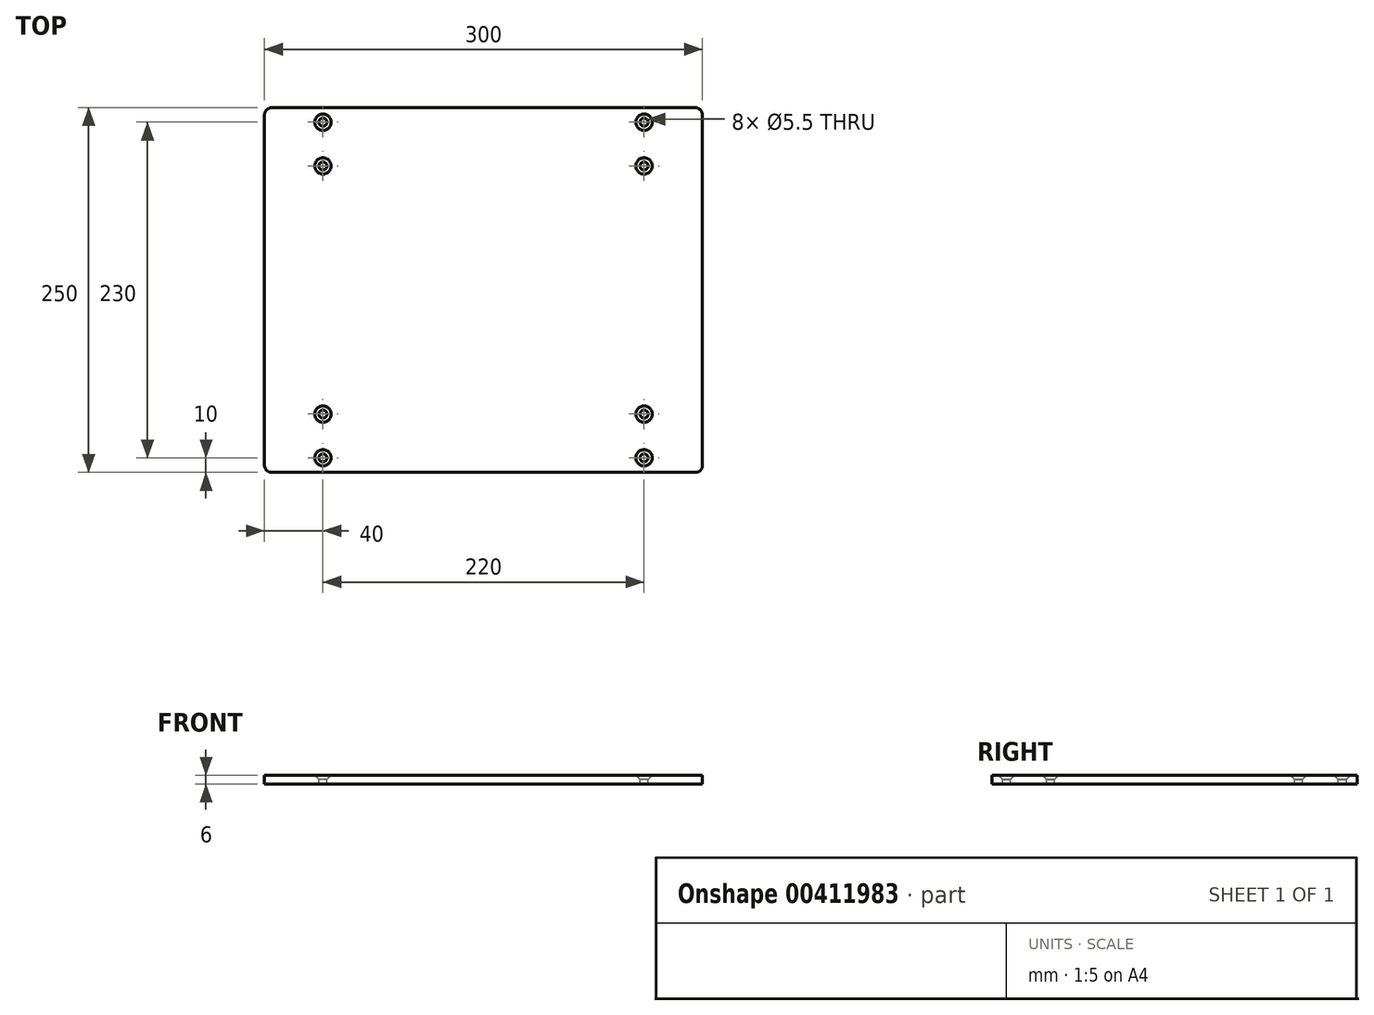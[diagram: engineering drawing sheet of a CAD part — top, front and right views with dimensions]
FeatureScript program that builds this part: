
annotation { "Feature Type Name" : "Feature", "Feature Type Description" : "" }
export const myFeature = defineFeature(function(context is Context, id is Id, definition is map)
    precondition{}
    {
        {
            var Q0;
            Q0=qCreatedBy(makeId("Top.planeOp"),FACE);
            var sketch = newSketch(context, id + "F0", { "sketchPlane" : qUnion([Q0])});
            skLineSegment(sketch, "E0.bottom", {"start": v(150, -125) * mm, "end": v(-150, -125) * mm});
            skLineSegment(sketch, "E0.top", {"start": v(150, 125) * mm, "end": v(-150, 125) * mm});
            skLineSegment(sketch, "E0.left", {"start": v(150, -125) * mm, "end": v(150, 125) * mm});
            skLineSegment(sketch, "E0.right", {"start": v(-150, -125) * mm, "end": v(-150, 125) * mm});
            skPoint(sketch, "E0.middle", {"position": v(0, 0) * mm});
            skLineSegment(sketch, "E1", {"start": v(-110, 125) * mm, "end": v(-110, -125) * mm, "construction": true});
            skLineSegment(sketch, "E2", {"start": v(110, 125) * mm, "end": v(110, -125) * mm, "construction": true});
            skPoint(sketch, "E3", {"position": v(-110, 115) * mm});
            skPoint(sketch, "E4", {"position": v(-110, 85) * mm});
            skPoint(sketch, "E5.MirrorP", {"position": v(110, 115) * mm});
            skPoint(sketch, "E6.MirrorP", {"position": v(110, 85) * mm});
            skPoint(sketch, "E7.MirrorP", {"position": v(-110, -85) * mm});
            skPoint(sketch, "E8.MirrorP", {"position": v(-110, -115) * mm});
            skPoint(sketch, "E9.MirrorP", {"position": v(110, -115) * mm});
            skPoint(sketch, "E10.MirrorP", {"position": v(110, -85) * mm});
            skSolve(sketch);
        }
        {
            var Q0;
            Q0 = qSketchRegion(id + "F0", true);
            extrude(context, id + "F1", {"entities" : qUnion([Q0]), "oppositeDirection" : true, "depth" : 6 * mm, "offsetDistance" : 25 * mm});
        }
        {
            var Q0;
            Q0=sQuery(id+"F0.wireOp",VERTEX,"E3");
            var Q1;
            Q1=sQuery(id+"F0.wireOp",VERTEX,"E4");
            var Q2;
            Q2=sQuery(id+"F0.wireOp",VERTEX,"E5.MirrorP");
            var Q3;
            Q3=sQuery(id+"F0.wireOp",VERTEX,"E6.MirrorP");
            var Q4;
            Q4=sQuery(id+"F0.wireOp",VERTEX,"E10.MirrorP");
            var Q5;
            Q5=sQuery(id+"F0.wireOp",VERTEX,"E9.MirrorP");
            var Q6;
            Q6=sQuery(id+"F0.wireOp",VERTEX,"E8.MirrorP");
            var Q7;
            Q7=sQuery(id+"F0.wireOp",VERTEX,"E7.MirrorP");
            var Q8;
            Q8=makeQuery(id+"F1.opExtrude","SWEPT_BODY",BODY,{"disambiguationData":[OSD([sQuery(id+"F0.wireOp",EDGE,"E0.bottom"),sQuery(id+"F0.wireOp",EDGE,"E0.top"),sQuery(id+"F0.wireOp",EDGE,"E0.left"),sQuery(id+"F0.wireOp",EDGE,"E0.right")])]});
            hole(context, id + "F2", {"style" : HoleStyle.C_SINK, "endStyle" : HoleEndStyle.THROUGH, "standardTappedOrClearance" : lookupTablePath({ "fit" : "Normal", "standard" : "ISO", "size" : "M5", "type" : "Clearance" }), "standardBlindInLast" : lookupTablePath({ "fit" : "Standard", "standard" : "ISO", "size" : "M5", "type" : "Clearance" }), "holeDiameter" : 5.5 * mm, "cSinkDiameter" : 11.2 * mm, "cSinkAngle" : 90 * degree, "majorDiameter" : 5 * mm, "isTappedThrough" : true, "tappedDepth" : 8 * mm, "tapClearance" : 3, "locations" : qUnion([Q0, Q1, Q2, Q3, Q4, Q5, Q6, Q7]), "scope" : qUnion([Q8])});
        }
        {
            var Q0;
            Q0=makeQuery(id+"F1.opExtrude","SWEPT_EDGE",EDGE,{"disambiguationData":[OSD([sQuery(id+"F0.wireOp",EDGE,"E0.top"),sQuery(id+"F0.wireOp",EDGE,"E0.right")])]});
            var Q1;
            Q1=makeQuery(id+"F1.opExtrude","SWEPT_EDGE",EDGE,{"disambiguationData":[OSD([sQuery(id+"F0.wireOp",EDGE,"E0.top"),sQuery(id+"F0.wireOp",EDGE,"E0.left")])]});
            var Q2;
            Q2=makeQuery(id+"F1.opExtrude","SWEPT_EDGE",EDGE,{"disambiguationData":[OSD([sQuery(id+"F0.wireOp",EDGE,"E0.bottom"),sQuery(id+"F0.wireOp",EDGE,"E0.left")])]});
            var Q3;
            Q3=makeQuery(id+"F1.opExtrude","SWEPT_EDGE",EDGE,{"disambiguationData":[OSD([sQuery(id+"F0.wireOp",EDGE,"E0.bottom"),sQuery(id+"F0.wireOp",EDGE,"E0.right")])]});
            fillet(context, id + "F3", {"entities" : qUnion([Q0, Q1, Q2, Q3]), "radius" : 5 * mm, "tangentPropagation" : true, "allowEdgeOverflow" : false});
        }
    });
